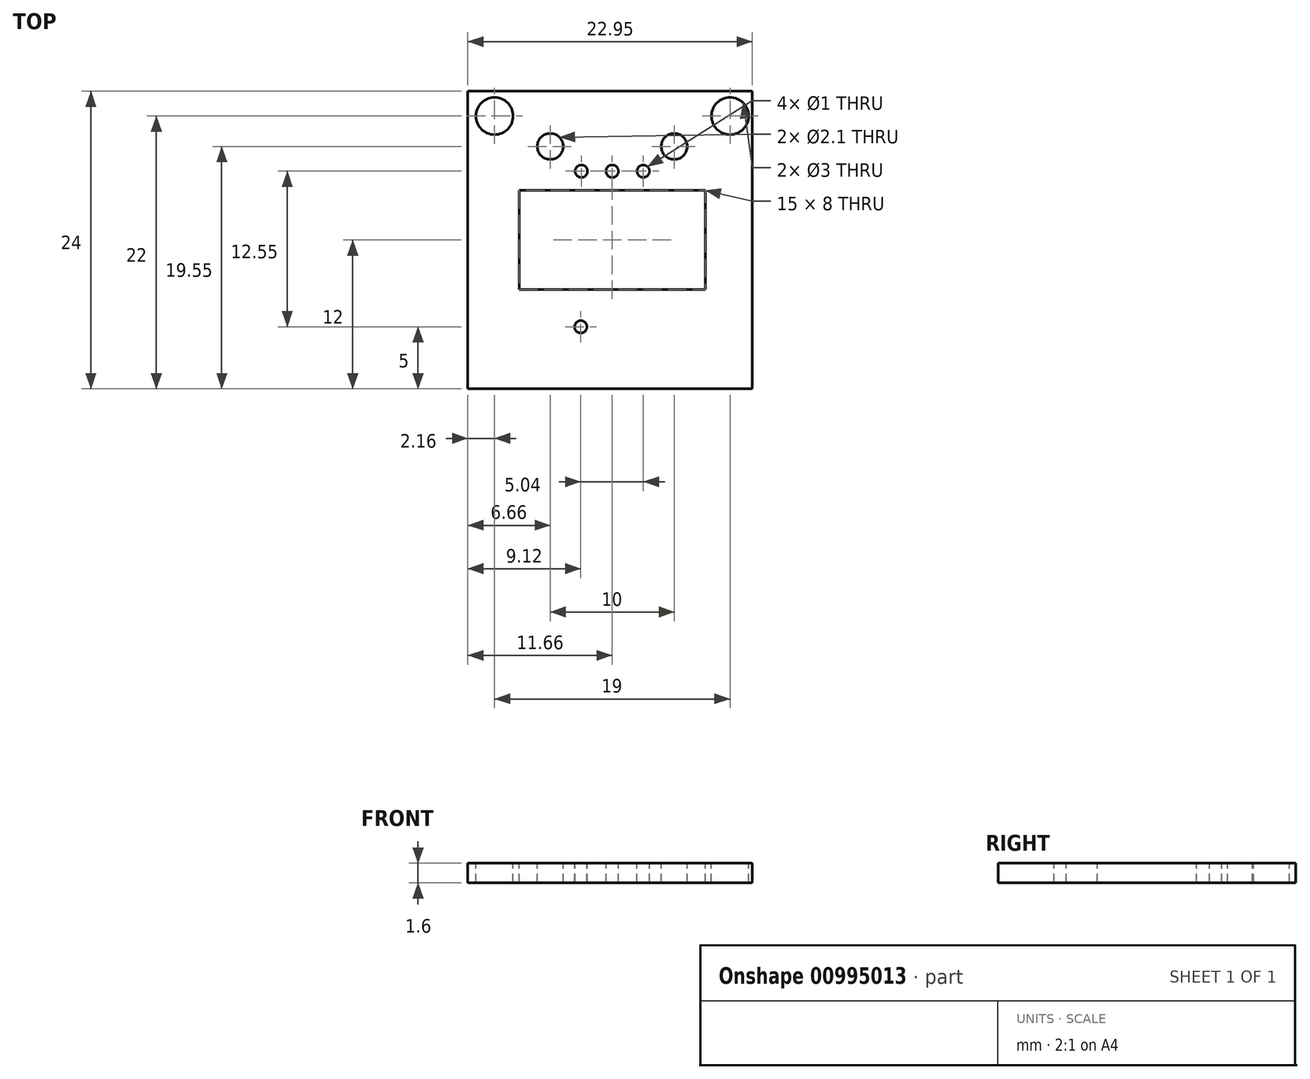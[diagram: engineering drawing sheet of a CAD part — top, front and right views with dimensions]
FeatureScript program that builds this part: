
annotation { "Feature Type Name" : "Feature", "Feature Type Description" : "" }
export const myFeature = defineFeature(function(context is Context, id is Id, definition is map)
    precondition{}
    {
        {
            var Q0;
            Q0=qCreatedBy(makeId("Top.planeOp"),FACE);
            var sketch = newSketch(context, id + "F0", { "sketchPlane" : qUnion([Q0])});
            skLineSegment(sketch, "E0.top", {"start": v(-11.66, -12) * mm, "end": v(11.3, -12) * mm});
            skLineSegment(sketch, "E0.left", {"start": v(-11.66, 12) * mm, "end": v(-11.66, -12) * mm});
            skLineSegment(sketch, "E0.right", {"start": v(11.3, 12) * mm, "end": v(11.3, -12) * mm});
            skCircle(sketch, "E1", {"center": v(0, 5.55) * mm, "radius": 0.5 * mm});
            skCircle(sketch, "E2", {"center": v(-2.5, 5.55) * mm, "radius": 0.5 * mm});
            skCircle(sketch, "E3", {"center": v(2.5, 5.55) * mm, "radius": 0.5 * mm});
            skCircle(sketch, "E4", {"center": v(-2.54, -7) * mm, "radius": 0.5 * mm});
            skLineSegment(sketch, "E5", {"start": v(0, 0.55) * mm, "end": v(0, 1.75) * mm});
            skPoint(sketch, "E6", {"position": v(0, 4.8) * mm});
            skCircle(sketch, "E7", {"center": v(-5, 7.55) * mm, "radius": 1.05 * mm});
            skCircle(sketch, "E8", {"center": v(5, 7.55) * mm, "radius": 1.05 * mm});
            skLineSegment(sketch, "E9", {"start": v(-11.66, 12) * mm, "end": v(11.3, 12) * mm});
            skSolve(sketch);
        }
        {
            var Q0;
            Q0=qSketchRegion(id+"F0",true);
            extrude(context, id + "F1", {"entities" : qUnion([Q0]), "oppositeDirection" : true, "depth" : 1.6 * mm, "offsetDistance" : 25 * mm});
        }
        {
            var Q0;
            Q0=makeQuery(id+"F1.opExtrude","CAP_FACE",FACE,{"disambiguationData":[OSD([sQuery(id+"F0.wireOp",EDGE,"E0.bottom"),sQuery(id+"F0.wireOp",EDGE,"E0.top"),sQuery(id+"F0.wireOp",EDGE,"E0.left"),sQuery(id+"F0.wireOp",EDGE,"E0.right"),sQuery(id+"F0.wireOp",EDGE,"E1"),sQuery(id+"F0.wireOp",EDGE,"E2"),sQuery(id+"F0.wireOp",EDGE,"E3"),sQuery(id+"F0.wireOp",EDGE,"E4"),sQuery(id+"F0.wireOp",EDGE,"9yhu0ApJ-A9Rv-WkGQ-m5Oh-gTQB5OdKfF1x.bottom"),sQuery(id+"F0.wireOp",EDGE,"9yhu0ApJ-A9Rv-WkGQ-m5Oh-gTQB5OdKfF1x.top"),sQuery(id+"F0.wireOp",EDGE,"9yhu0ApJ-A9Rv-WkGQ-m5Oh-gTQB5OdKfF1x.left"),sQuery(id+"F0.wireOp",EDGE,"9yhu0ApJ-A9Rv-WkGQ-m5Oh-gTQB5OdKfF1x.right"),sQuery(id+"F0.wireOp",EDGE,"05f9d2f0-11d9-4e1b-b2fe-26b268615fe30.MirrorCS"),sQuery(id+"F0.wireOp",EDGE,"05f9d2f0-11d9-4e1b-b2fe-26b268615fe31.MirrorCS"),sQuery(id+"F0.wireOp",EDGE,"05f9d2f0-11d9-4e1b-b2fe-26b268615fe32.MirrorCS"),sQuery(id+"F0.wireOp",EDGE,"05f9d2f0-11d9-4e1b-b2fe-26b268615fe33.MirrorCS")])],"isStart":true});
            var sketch = newSketch(context, id + "F2", { "sketchPlane" : qUnion([Q0])});
            skLineSegment(sketch, "E10.bottom", {"start": v(7.5, 4) * mm, "end": v(-7.5, 4) * mm});
            skLineSegment(sketch, "E10.top", {"start": v(7.5, -4) * mm, "end": v(-7.5, -4) * mm});
            skLineSegment(sketch, "E10.left", {"start": v(7.5, 4) * mm, "end": v(7.5, -4) * mm});
            skLineSegment(sketch, "E10.right", {"start": v(-7.5, 4) * mm, "end": v(-7.5, -4) * mm});
            skPoint(sketch, "E10.middle", {"position": v(0, 0) * mm});
            skSolve(sketch);
        }
        {
            var Q0;
            Q0=qSketchRegion(id+"F2",true);
            extrude(context, id + "F3", {"entities" : qUnion([Q0]), "operationType" : NewBodyOperationType.REMOVE, "oppositeDirection" : true, "depth" : 25 * mm, "offsetDistance" : 25 * mm});
        }
        {
            var Q0;
            Q0=makeQuery(id+"F1.opExtrude","CAP_FACE",FACE,{"disambiguationData":[OSD([sQuery(id+"F0.wireOp",EDGE,"E0.top"),sQuery(id+"F0.wireOp",EDGE,"E0.left"),sQuery(id+"F0.wireOp",EDGE,"E0.right"),sQuery(id+"F0.wireOp",EDGE,"E1"),sQuery(id+"F0.wireOp",EDGE,"E2"),sQuery(id+"F0.wireOp",EDGE,"E3"),sQuery(id+"F0.wireOp",EDGE,"E4"),sQuery(id+"F0.wireOp",EDGE,"E7"),sQuery(id+"F0.wireOp",EDGE,"E8"),sQuery(id+"F0.wireOp",EDGE,"E9")])],"isStart":true});
            var sketch = newSketch(context, id + "F4", { "sketchPlane" : qUnion([Q0])});
            skCircle(sketch, "E11", {"center": v(-9.5, 10) * mm, "radius": 1.5 * mm});
            skCircle(sketch, "E12.MirrorC", {"center": v(9.5, 10) * mm, "radius": 1.5 * mm});
            skSolve(sketch);
        }
        {
            var Q0;
            Q0 = qSketchRegion(id + "F4", true);
            extrude(context, id + "F5", {"entities" : qUnion([Q0]), "operationType" : NewBodyOperationType.REMOVE, "oppositeDirection" : true, "depth" : 25 * mm, "offsetDistance" : 25 * mm});
        }
    });
